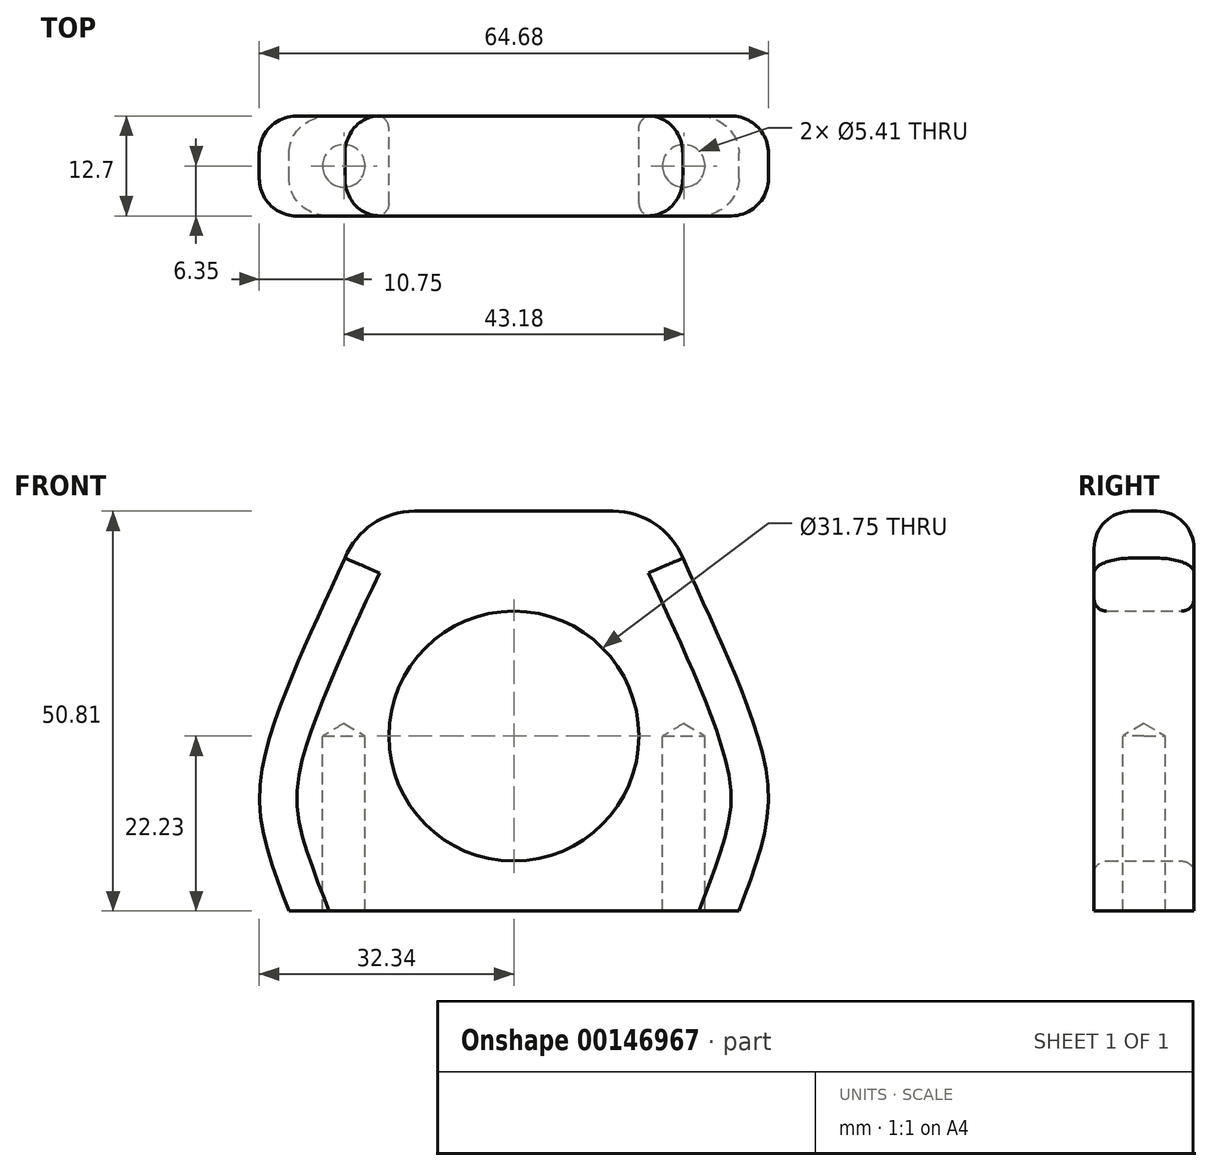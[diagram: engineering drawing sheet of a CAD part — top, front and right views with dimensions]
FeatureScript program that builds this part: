
annotation { "Feature Type Name" : "Feature", "Feature Type Description" : "" }
export const myFeature = defineFeature(function(context is Context, id is Id, definition is map)
    precondition{}
    {
        {
            var Q0;
            Q0=qCreatedBy(makeId("Front.planeOp"),FACE);
            var sketch = newSketch(context, id + "F0", { "sketchPlane" : qUnion([Q0])});
            skCircle(sketch, "E0", {"center": v(0, 0) * mm, "radius": 15.88 * mm});
            skLineSegment(sketch, "E1", {"start": v(0, -22.23) * mm, "end": v(28.58, -22.23) * mm});
            skLineSegment(sketch, "E2", {"start": v(28.58, -12.7) * mm, "end": v(31.75, -12.7) * mm, "construction": true});
            skLineSegment(sketch, "E3", {"start": v(0, 28.58) * mm, "end": v(12.62, 28.58) * mm});
            skPoint(sketch, "E4.visualSharp", {"position": v(19.05, 28.58) * mm});
            skArc(sketch, "E4.filletArc", {"start": v(21.45, 22.6) * mm, "mid": v(17.95, 26.94) * mm, "end": v(12.62, 28.58) * mm});
            skFitSpline(sketch, "E5", {"points": [v(28.58, -22.23) * mm, v(31.75, -12.7) * mm, v(31.75, -2.96) * mm, v(21.45, 22.6) * mm], "startDerivative": vector(13.5, 35.33) * mm, "endDerivative": vector(-29.13, 62.72) * mm});
            skLineSegment(sketch, "E6.MirrorCS", {"start": v(0, 28.58) * mm, "end": v(-12.62, 28.58) * mm});
            skArc(sketch, "E7.MirrorCS", {"start": v(-21.45, 22.6) * mm, "mid": v(-17.95, 26.94) * mm, "end": v(-12.62, 28.58) * mm});
            skFitSpline(sketch, "E8.MirrorCS", {"points": [v(-28.58, -22.23) * mm, v(-31.75, -12.7) * mm, v(-31.75, -2.96) * mm, v(-21.45, 22.6) * mm], "startDerivative": vector(-13.5, 35.33) * mm, "endDerivative": vector(29.13, 62.72) * mm});
            skLineSegment(sketch, "E9.MirrorCS", {"start": v(0, -22.23) * mm, "end": v(-28.58, -22.23) * mm});
            skSolve(sketch);
        }
        {
            var Q0;
            Q0=makeQuery(id+"F0.imprint","IMPRINT",FACE,{"disambiguationData":[TD([[makeQuery(id+"F0.imprint","IMPRINT",EDGE,{"derivedFrom":sQuery(id+"F0.wireOp",EDGE,"E0")}),-1.0]])]});
            extrude(context, id + "F1", {"entities" : qUnion([Q0]), "depth" : 12.7 * mm});
        }
        {
            var Q0;
            Q0=makeQuery(id+"F1.opExtrude","CAP_EDGE",EDGE,{"disambiguationData":[OSD([sQuery(id+"F0.wireOp",EDGE,"E8.MirrorCS")])],"isStart":false});
            var Q1;
            Q1=makeQuery(id+"F1.opExtrude","CAP_EDGE",EDGE,{"disambiguationData":[OSD([sQuery(id+"F0.wireOp",EDGE,"E3"),sQuery(id+"F0.wireOp",EDGE,"E6.MirrorCS")])],"isStart":false});
            var Q2;
            Q2=makeQuery(id+"F1.opExtrude","CAP_EDGE",EDGE,{"disambiguationData":[OSD([sQuery(id+"F0.wireOp",EDGE,"E7.MirrorCS")])],"isStart":false});
            var Q3;
            Q3=makeQuery(id+"F1.opExtrude","CAP_EDGE",EDGE,{"disambiguationData":[OSD([sQuery(id+"F0.wireOp",EDGE,"E4.filletArc")])],"isStart":false});
            var Q4;
            Q4=makeQuery(id+"F1.opExtrude","CAP_EDGE",EDGE,{"disambiguationData":[OSD([sQuery(id+"F0.wireOp",EDGE,"E5")])],"isStart":false});
            var Q5;
            Q5=makeQuery(id+"F1.opExtrude","CAP_EDGE",EDGE,{"disambiguationData":[OSD([sQuery(id+"F0.wireOp",EDGE,"E8.MirrorCS")])],"isStart":true});
            var Q6;
            Q6=makeQuery(id+"F1.opExtrude","CAP_EDGE",EDGE,{"disambiguationData":[OSD([sQuery(id+"F0.wireOp",EDGE,"E7.MirrorCS")])],"isStart":true});
            var Q7;
            Q7=makeQuery(id+"F1.opExtrude","CAP_EDGE",EDGE,{"disambiguationData":[OSD([sQuery(id+"F0.wireOp",EDGE,"E3"),sQuery(id+"F0.wireOp",EDGE,"E6.MirrorCS")])],"isStart":true});
            var Q8;
            Q8=makeQuery(id+"F1.opExtrude","CAP_EDGE",EDGE,{"disambiguationData":[OSD([sQuery(id+"F0.wireOp",EDGE,"E4.filletArc")])],"isStart":true});
            var Q9;
            Q9=makeQuery(id+"F1.opExtrude","CAP_EDGE",EDGE,{"disambiguationData":[OSD([sQuery(id+"F0.wireOp",EDGE,"E5")])],"isStart":true});
            fillet(context, id + "F2", {"entities" : qUnion([Q0, Q1, Q2, Q3, Q4, Q5, Q6, Q7, Q8, Q9]), "radius" : 4.75 * mm, "width" : 5.08 * mm, "tangentPropagation" : true, "blendControlType" : BlendControlType.RADIUS, "defaultsChanged" : true, "isAsymmetric" : false, "otherRadius" : 5.08 * mm, "flipAsymmetric" : false, "isPartial" : false, "partialFirstEdgeTotalParameter" : 0.01, "partialOppositeParameter" : true, "secondBound" : false, "partialSecondEdgeTotalParameter" : 0.99, "vertexSettings" : [], "pointOnEdgeSettings" : [], "allowEdgeOverflow" : false, "smoothCorners" : false, "filletType" : FilletType.EDGE});
        }
        {
            var Q0;
            Q0=makeQuery(id+"F1.opExtrude","CAP_EDGE",EDGE,{"disambiguationData":[OSD([sQuery(id+"F0.wireOp",EDGE,"E0")])],"isStart":true});
            var Q1;
            Q1=makeQuery(id+"F1.opExtrude","CAP_EDGE",EDGE,{"disambiguationData":[OSD([sQuery(id+"F0.wireOp",EDGE,"E0")])],"isStart":false});
            fillet(context, id + "F3", {"entities" : qUnion([Q0, Q1]), "radius" : 1.59 * mm, "tangentPropagation" : true, "allowEdgeOverflow" : false});
        }
        {
            var Q0;
            Q0=makeQuery(id+"F1.opExtrude","SWEPT_FACE",FACE,{"disambiguationData":[OSD([sQuery(id+"F0.wireOp",EDGE,"E1"),sQuery(id+"F0.wireOp",EDGE,"E9.MirrorCS")])]});
            var sketch = newSketch(context, id + "F4", { "sketchPlane" : qUnion([Q0]), "disableImprinting" : false});
            skPoint(sketch, "E10", {"position": v(21.59, 6.35) * mm});
            skPoint(sketch, "E11", {"position": v(-21.59, 6.35) * mm});
            skSolve(sketch);
        }
        {
            var Q0;
            Q0=sQuery(id+"F4.wireOp",VERTEX,"E11");
            var Q1;
            Q1=sQuery(id+"F4.wireOp",VERTEX,"E10");
            var Q2;
            Q2=makeQuery(id+"F1.opExtrude","SWEPT_BODY",BODY,{"disambiguationData":[OSD([sQuery(id+"F0.wireOp",EDGE,"E0"),sQuery(id+"F0.wireOp",EDGE,"E1"),sQuery(id+"F0.wireOp",EDGE,"E3"),sQuery(id+"F0.wireOp",EDGE,"E4.filletArc"),sQuery(id+"F0.wireOp",EDGE,"E5"),sQuery(id+"F0.wireOp",EDGE,"E6.MirrorCS"),sQuery(id+"F0.wireOp",EDGE,"E7.MirrorCS"),sQuery(id+"F0.wireOp",EDGE,"E8.MirrorCS"),sQuery(id+"F0.wireOp",EDGE,"E9.MirrorCS")])]});
            hole(context, id + "F5", {"style" : HoleStyle.SIMPLE, "endStyle" : HoleEndStyle.BLIND, "standardTappedOrClearance" : lookupTablePath({ "standard" : "ANSI", "engagement" : "75%", "pitch" : "28 tpi", "size" : "1/4", "type" : "Tapped" }), "standardBlindInLast" : lookupTablePath({ "standard" : "ANSI", "fit" : "Free", "engagement" : "75%", "pitch" : "28 tpi", "size" : "1/4", "type" : "Clearance & tapped" }), "holeDiameter" : 5.4 * mm, "holeDepth" : 22.22 * mm, "startFromSketch" : true, "locations" : qUnion([Q0, Q1]), "scope" : qUnion([Q2]), "tappedDepth" : 21.59 * mm, "tappedAngle" : 1.79 * degree, "tapClearance" : 0.7, "majorDiameter" : 6.35 * mm, "showTappedDepth" : true});
        }
    });
